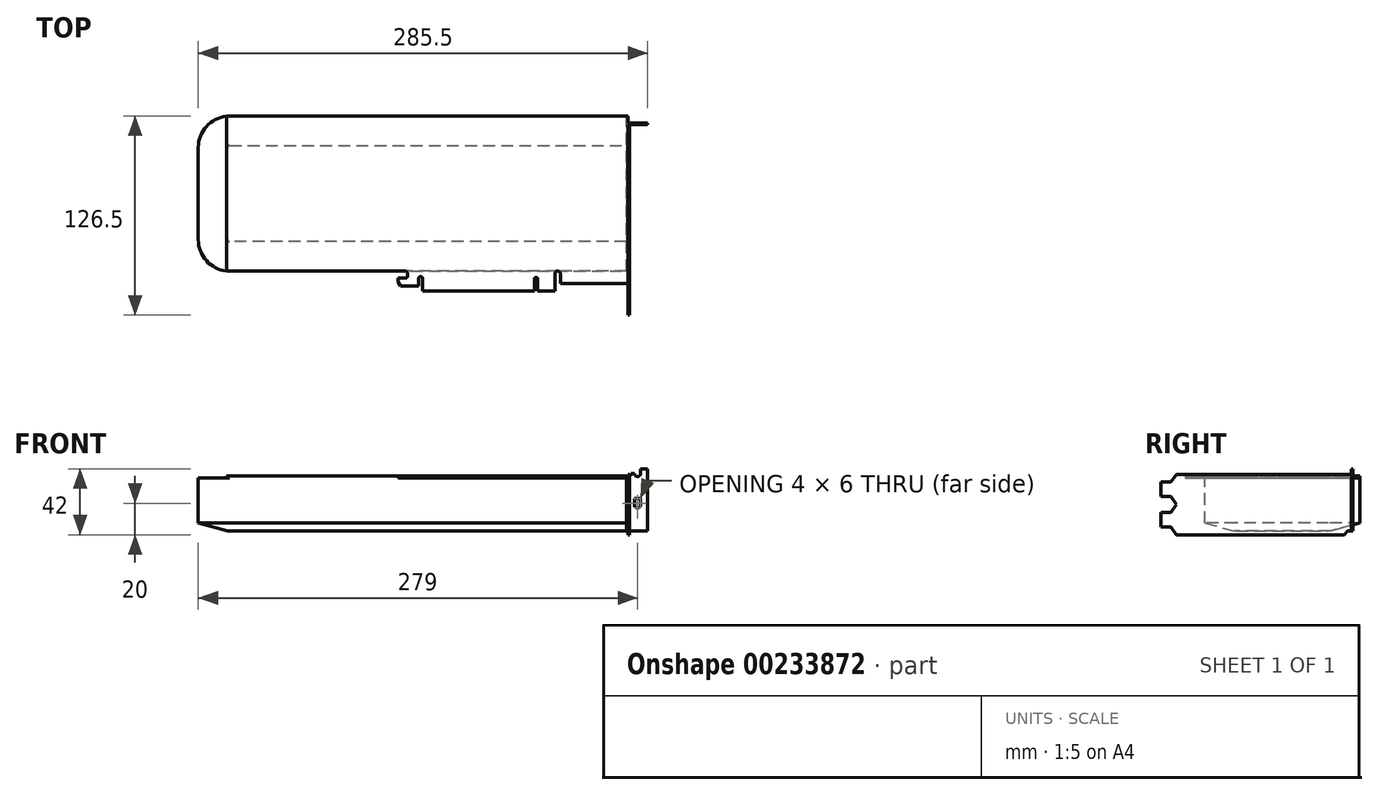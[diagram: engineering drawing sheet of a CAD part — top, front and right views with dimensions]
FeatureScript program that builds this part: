
annotation { "Feature Type Name" : "Feature", "Feature Type Description" : "" }
export const myFeature = defineFeature(function(context is Context, id is Id, definition is map)
    precondition{}
    {
        {
            var Q0;
            Q0=qCreatedBy(makeId("Top.planeOp"),FACE);
            var sketch = newSketch(context, id + "F0", { "sketchPlane" : qUnion([Q0])});
            skLineSegment(sketch, "E0.bottom", {"start": v(127.5, -53.25) * mm, "end": v(84.5, -53.25) * mm});
            skLineSegment(sketch, "E0.top", {"start": v(127.5, 53.25) * mm, "end": v(-127.5, 53.25) * mm});
            skLineSegment(sketch, "E0.left", {"start": v(127.5, -53.25) * mm, "end": v(127.5, 53.25) * mm});
            skLineSegment(sketch, "E0.right", {"start": v(-127.5, -45.25) * mm, "end": v(-127.5, 53.25) * mm});
            skPoint(sketch, "E0.middle", {"position": v(0, 0) * mm});
            skLineSegment(sketch, "E1", {"start": v(81, -45.25) * mm, "end": v(81, -57.75) * mm});
            skLineSegment(sketch, "E2", {"start": v(81, -57.75) * mm, "end": v(70, -57.75) * mm});
            skLineSegment(sketch, "E3", {"start": v(70, -57.75) * mm, "end": v(70, -49.25) * mm});
            skLineSegment(sketch, "E4", {"start": v(68, -49.25) * mm, "end": v(68, -57.75) * mm});
            skLineSegment(sketch, "E5", {"start": v(68, -57.75) * mm, "end": v(-3, -57.75) * mm});
            skLineSegment(sketch, "E6.trimOffspring", {"start": v(-5.5, -54.75) * mm, "end": v(-17, -54.75) * mm});
            skLineSegment(sketch, "E7", {"start": v(68, -49.25) * mm, "end": v(70, -49.25) * mm});
            skLineSegment(sketch, "E8", {"start": v(84.5, -53.25) * mm, "end": v(84.5, -45.25) * mm});
            skLineSegment(sketch, "E9", {"start": v(84.5, -45.25) * mm, "end": v(81, -45.25) * mm});
            skLineSegment(sketch, "E10", {"start": v(-5.5, -54.75) * mm, "end": v(-5.5, -48.75) * mm});
            skLineSegment(sketch, "E11", {"start": v(-5.5, -48.75) * mm, "end": v(-3, -48.75) * mm});
            skLineSegment(sketch, "E12", {"start": v(-3, -48.75) * mm, "end": v(-3, -57.75) * mm});
            skLineSegment(sketch, "E13", {"start": v(-17, -54.75) * mm, "end": v(-18.5, -52.25) * mm});
            skLineSegment(sketch, "E14", {"start": v(-18.5, -52.25) * mm, "end": v(-18.5, -49.75) * mm});
            skLineSegment(sketch, "E15", {"start": v(-18.5, -49.75) * mm, "end": v(-12.5, -49.75) * mm});
            skLineSegment(sketch, "E16", {"start": v(-12.5, -49.75) * mm, "end": v(-12.5, -45.25) * mm});
            skLineSegment(sketch, "E17", {"start": v(-12.5, -45.25) * mm, "end": v(-127.5, -45.25) * mm});
            skSolve(sketch);
        }
        {
            var Q0;
            Q0 = qSketchRegion(id + "F0", true);
            extrude(context, id + "F1", {"entities" : qUnion([Q0]), "depth" : 1.5 * mm});
        }
        {
            var Q0;
            Q0=makeQuery(id+"F1.opExtrude","SWEPT_FACE",FACE,{"disambiguationData":[OSD([sQuery(id+"F0.wireOp",EDGE,"E0.left")])]});
            var sketch = newSketch(context, id + "F2", { "sketchPlane" : qUnion([Q0])});
            skLineSegment(sketch, "E18.bottom", {"start": v(-63.25, 2.5) * mm, "end": v(47.75, 2.5) * mm});
            skLineSegment(sketch, "E18.top", {"start": v(-63.25, -36) * mm, "end": v(43.25, -36) * mm});
            skLineSegment(sketch, "E18.left", {"start": v(-73.25, -2.5) * mm, "end": v(-73.25, -11.75) * mm});
            skLineSegment(sketch, "E18.right", {"start": v(47.75, 2.5) * mm, "end": v(47.75, -33.5) * mm});
            skLineSegment(sketch, "E19", {"start": v(-73.25, -11.75) * mm, "end": v(-66.75, -11.75) * mm});
            skLineSegment(sketch, "E20", {"start": v(-66.75, -11.75) * mm, "end": v(-63.25, -16.75) * mm});
            skLineSegment(sketch, "E21", {"start": v(-63.25, -16.75) * mm, "end": v(-66.75, -21.75) * mm});
            skLineSegment(sketch, "E22", {"start": v(-66.75, -21.75) * mm, "end": v(-73.25, -21.75) * mm});
            skLineSegment(sketch, "E23.trimOffspring", {"start": v(-73.25, -21.75) * mm, "end": v(-73.25, -31) * mm});
            skLineSegment(sketch, "E24", {"start": v(-73.25, -31) * mm, "end": v(-66.75, -31) * mm});
            skLineSegment(sketch, "E25", {"start": v(-66.75, -31) * mm, "end": v(-63.25, -36) * mm});
            skLineSegment(sketch, "E26", {"start": v(-73.25, -2.5) * mm, "end": v(-66.75, -2.5) * mm});
            skLineSegment(sketch, "E27", {"start": v(-66.75, -2.5) * mm, "end": v(-63.25, 2.5) * mm});
            skLineSegment(sketch, "E28", {"start": v(43.25, -36) * mm, "end": v(45.25, -33.5) * mm});
            skLineSegment(sketch, "E29", {"start": v(45.25, -33.5) * mm, "end": v(47.75, -33.5) * mm});
            skSolve(sketch);
        }
        {
            var Q0;
            Q0 = qSketchRegion(id + "F2", true);
            extrude(context, id + "F3", {"entities" : qUnion([Q0]), "operationType" : NewBodyOperationType.ADD, "depth" : 1 * mm});
        }
        {
            var Q0;
            Q0=makeQuery(id+"F1.opExtrude","SWEPT_EDGE",EDGE,{"disambiguationData":[OSD([sQuery(id+"F0.wireOp",EDGE,"E4"),sQuery(id+"F0.wireOp",EDGE,"E7")])]});
            var Q1;
            Q1=makeQuery(id+"F1.opExtrude","SWEPT_EDGE",EDGE,{"disambiguationData":[OSD([sQuery(id+"F0.wireOp",EDGE,"E3"),sQuery(id+"F0.wireOp",EDGE,"E7")])]});
            fillet(context, id + "F4", {"entities" : qUnion([Q0, Q1]), "radius" : 1 * mm, "tangentPropagation" : true, "allowEdgeOverflow" : false});
        }
        {
            var Q0;
            Q0=makeQuery(id+"F1.opExtrude","SWEPT_EDGE",EDGE,{"disambiguationData":[OSD([sQuery(id+"F0.wireOp",EDGE,"E1"),sQuery(id+"F0.wireOp",EDGE,"E9")])]});
            var Q1;
            Q1=makeQuery(id+"F1.opExtrude","SWEPT_EDGE",EDGE,{"disambiguationData":[OSD([sQuery(id+"F0.wireOp",EDGE,"E8"),sQuery(id+"F0.wireOp",EDGE,"E9")])]});
            fillet(context, id + "F5", {"entities" : qUnion([Q0, Q1]), "radius" : 1.75 * mm, "tangentPropagation" : true, "allowEdgeOverflow" : false});
        }
        {
            var Q0;
            Q0=makeQuery(id+"F1.opExtrude","SWEPT_EDGE",EDGE,{"disambiguationData":[OSD([sQuery(id+"F0.wireOp",EDGE,"E10"),sQuery(id+"F0.wireOp",EDGE,"E11")])]});
            var Q1;
            Q1=makeQuery(id+"F1.opExtrude","SWEPT_EDGE",EDGE,{"disambiguationData":[OSD([sQuery(id+"F0.wireOp",EDGE,"E11"),sQuery(id+"F0.wireOp",EDGE,"E12")])]});
            fillet(context, id + "F6", {"entities" : qUnion([Q0, Q1]), "radius" : 1.25 * mm, "tangentPropagation" : true, "allowEdgeOverflow" : false});
        }
        {
            var Q0;
            Q0=makeQuery(id+"F1.opExtrude","SWEPT_EDGE",EDGE,{"disambiguationData":[OSD([sQuery(id+"F0.wireOp",EDGE,"E15"),sQuery(id+"F0.wireOp",EDGE,"E16")])]});
            var Q1;
            Q1=makeQuery(id+"F1.opExtrude","SWEPT_EDGE",EDGE,{"disambiguationData":[OSD([sQuery(id+"F0.wireOp",EDGE,"E16"),sQuery(id+"F0.wireOp",EDGE,"E17")])]});
            fillet(context, id + "F7", {"entities" : qUnion([Q0, Q1]), "radius" : 1.5 * mm, "tangentPropagation" : true, "allowEdgeOverflow" : false});
        }
        {
            var Q0;
            Q0=makeQuery(id+"F3.opExtrude","SWEPT_FACE",FACE,{"disambiguationData":[OSD([sQuery(id+"F2.wireOp",EDGE,"E18.right")])]});
            var sketch = newSketch(context, id + "F8", { "sketchPlane" : qUnion([Q0])});
            skLineSegment(sketch, "E30.bottom", {"start": v(-127.5, -33.5) * mm, "end": v(-140, -33.5) * mm});
            skLineSegment(sketch, "E30.left", {"start": v(-127.5, -33.5) * mm, "end": v(-127.5, 1.5) * mm});
            skLineSegment(sketch, "E30.right", {"start": v(-140, -33.5) * mm, "end": v(-140, 6) * mm});
            skLineSegment(sketch, "E31", {"start": v(-129.5, 1.5) * mm, "end": v(-129.5, 3) * mm});
            skLineSegment(sketch, "E32", {"start": v(-129.5, 3) * mm, "end": v(-131.5, 3) * mm});
            skLineSegment(sketch, "E33", {"start": v(-129.5, 1.5) * mm, "end": v(-127.5, 1.5) * mm});
            skLineSegment(sketch, "E34", {"start": v(-140, 6) * mm, "end": v(-135.5, 6) * mm});
            skArc(sketch, "E35", {"start": v(-135.5, 3) * mm, "mid": v(-133.5, 1) * mm, "end": v(-131.5, 3) * mm});
            skLineSegment(sketch, "E36", {"start": v(-135.5, 6) * mm, "end": v(-135.5, 3) * mm});
            skLineSegment(sketch, "E37", {"start": v(-135.5, -13) * mm, "end": v(-131.5, -13) * mm});
            skLineSegment(sketch, "E38", {"start": v(-131.5, -13) * mm, "end": v(-131.5, -17) * mm});
            skLineSegment(sketch, "E39", {"start": v(-135.5, -13) * mm, "end": v(-135.5, -17) * mm});
            skArc(sketch, "E40", {"start": v(-135.5, -17) * mm, "mid": v(-133.5, -19) * mm, "end": v(-131.5, -17) * mm});
            skSolve(sketch);
        }
        {
            var Q0;
            Q0 = qSketchRegion(id + "F8", true);
            extrude(context, id + "F9", {"entities" : qUnion([Q0]), "operationType" : NewBodyOperationType.ADD, "depth" : 1 * mm});
        }
        {
            var Q0;
            Q0=makeQuery(id+"F1.opExtrude","CAP_FACE",FACE,{"disambiguationData":[OSD([sQuery(id+"F0.wireOp",EDGE,"E0.bottom"),sQuery(id+"F0.wireOp",EDGE,"E0.top"),sQuery(id+"F0.wireOp",EDGE,"E0.left"),sQuery(id+"F0.wireOp",EDGE,"E0.right"),sQuery(id+"F0.wireOp",EDGE,"E1"),sQuery(id+"F0.wireOp",EDGE,"E2"),sQuery(id+"F0.wireOp",EDGE,"E3"),sQuery(id+"F0.wireOp",EDGE,"E4"),sQuery(id+"F0.wireOp",EDGE,"E5"),sQuery(id+"F0.wireOp",EDGE,"E6.trimOffspring"),sQuery(id+"F0.wireOp",EDGE,"E7"),sQuery(id+"F0.wireOp",EDGE,"E8"),sQuery(id+"F0.wireOp",EDGE,"E9"),sQuery(id+"F0.wireOp",EDGE,"E10"),sQuery(id+"F0.wireOp",EDGE,"E11"),sQuery(id+"F0.wireOp",EDGE,"E12"),sQuery(id+"F0.wireOp",EDGE,"E13"),sQuery(id+"F0.wireOp",EDGE,"E14"),sQuery(id+"F0.wireOp",EDGE,"E15"),sQuery(id+"F0.wireOp",EDGE,"E16"),sQuery(id+"F0.wireOp",EDGE,"E17")])],"isStart":true});
            var sketch = newSketch(context, id + "F10", { "sketchPlane" : qUnion([Q0])});
            skLineSegment(sketch, "E41.bottom", {"start": v(126.5, 45.25) * mm, "end": v(-125.5, 45.25) * mm});
            skLineSegment(sketch, "E41.top", {"start": v(126.5, -53.25) * mm, "end": v(-125.5, -53.25) * mm});
            skLineSegment(sketch, "E41.left", {"start": v(126.5, 45.25) * mm, "end": v(126.5, -53.25) * mm});
            skLineSegment(sketch, "E41.right", {"start": v(-145.5, 25.25) * mm, "end": v(-145.5, -33.25) * mm});
            skPoint(sketch, "E42.visualSharp", {"position": v(-145.5, 45.25) * mm});
            skArc(sketch, "E42.filletArc", {"start": v(-125.5, 45.25) * mm, "mid": v(-139.64, 39.4) * mm, "end": v(-145.5, 25.25) * mm});
            skPoint(sketch, "E43.visualSharp", {"position": v(-145.5, -53.25) * mm});
            skArc(sketch, "E43.filletArc", {"start": v(-145.5, -33.25) * mm, "mid": v(-139.64, -47.4) * mm, "end": v(-125.5, -53.25) * mm});
            skSolve(sketch);
        }
        {
            var Q0;
            Q0 = qSketchRegion(id + "F10", true);
            var Q1;
            Q1=makeQuery(id+"F9.boolean.opBoolean","MERGE",FACE,{"derivedFrom":[makeQuery(id+"F3.opExtrude","SWEPT_FACE",FACE,{"disambiguationData":[OSD([sQuery(id+"F2.wireOp",EDGE,"E29")])]}),makeQuery(id+"F9.opExtrude","SWEPT_FACE",FACE,{"disambiguationData":[OSD([sQuery(id+"F8.wireOp",EDGE,"E30.bottom")])]})]});
            extrude(context, id + "F11", {"entities" : qUnion([Q0]), "operationType" : NewBodyOperationType.ADD, "endBound" : BoundingType.UP_TO_SURFACE, "depth" : 25 * mm, "endBoundEntityFace" : qUnion([Q1]), "offsetDistance" : 25 * mm});
        }
        {
            var Q0;
            Q0=makeQuery(id+"F11.opExtrude","CAP_EDGE",EDGE,{"disambiguationData":[OSD([sQuery(id+"F10.wireOp",EDGE,"E41.bottom")])],"isStart":false});
            var Q1;
            Q1=makeQuery(id+"F11.opExtrude","CAP_EDGE",EDGE,{"disambiguationData":[OSD([sQuery(id+"F10.wireOp",EDGE,"E41.top")])],"isStart":false});
            chamfer(context, id + "F12", {"entities" : qUnion([Q0, Q1]), "chamferType" : ChamferType.OFFSET_ANGLE, "width" : 5 * mm, "oppositeDirection" : false, "angle" : 75 * degree, "tangentPropagation" : true});
        }
    });
